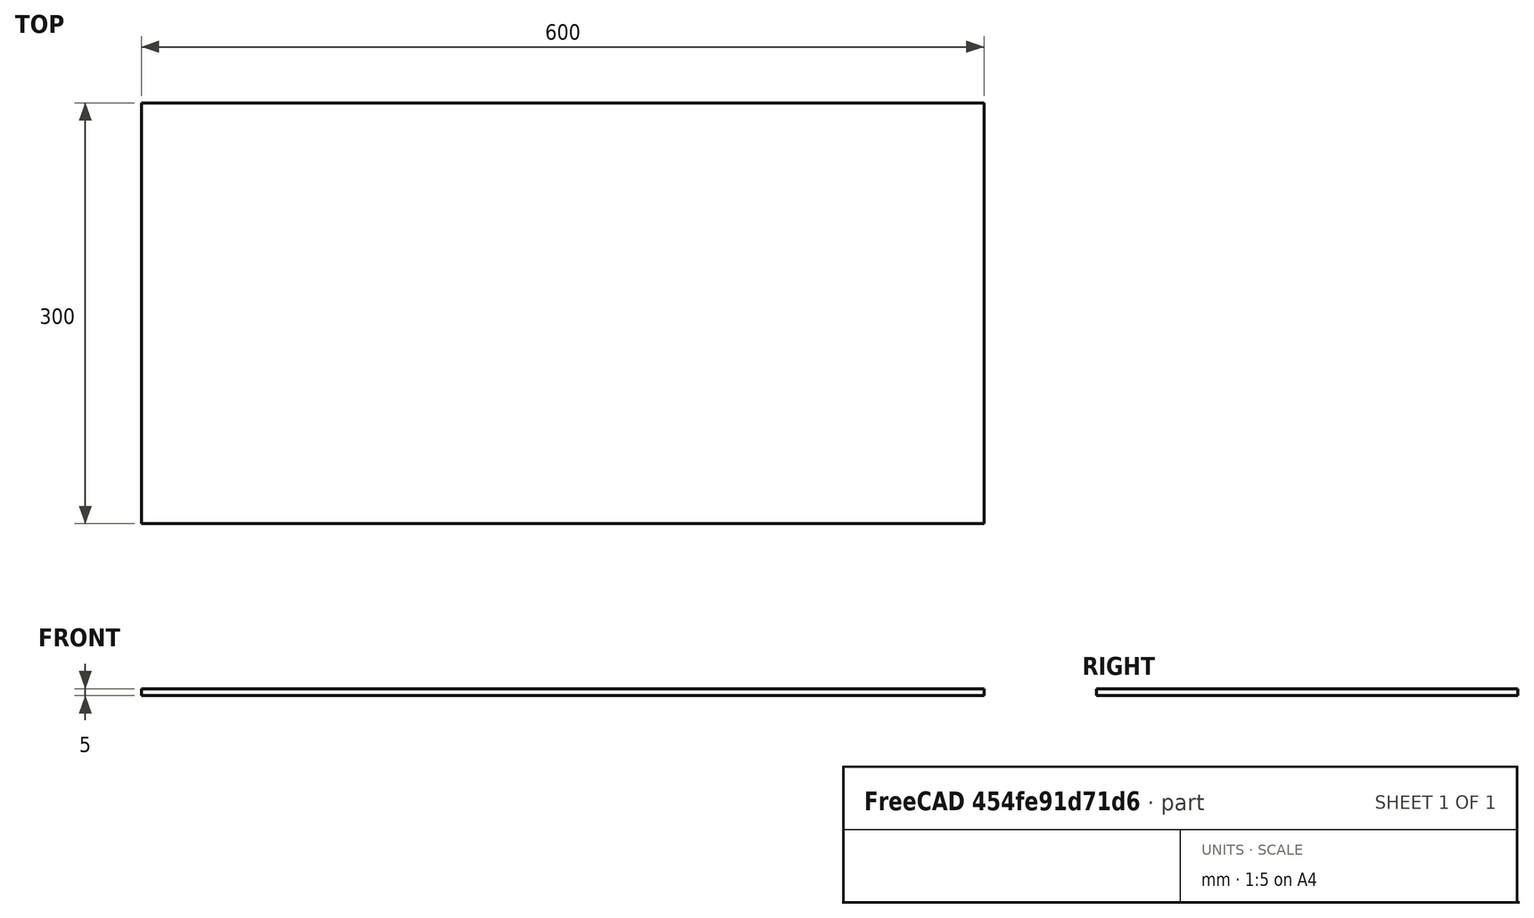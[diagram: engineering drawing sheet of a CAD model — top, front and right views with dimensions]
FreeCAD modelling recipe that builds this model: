
FCSTD DOCUMENT  (FreeCAD 0.19R16694 (Git))
Label: window-acryl-600x300
License: Public Domain
LicenseURL: http://en.wikipedia.org/wiki/Public_domain
objects: Sketcher::SketchObject×1, PartDesign::Pad×1, PartDesign::Body×1
note: 4 computed .brp shape members not serialized (recipe doc carries the construction recipe); baked Part::Feature solids carry a one-line shape summary decoded from their .brp

FEATURE [Sketcher::SketchObject] Sketch
  MapMode = 5
  Support = -> [XY_Plane]
  sketch-geometry (4):
    g0: LineSegment StartX=-300 StartY=150 StartZ=0 EndX=300 EndY=150 EndZ=0
    g1: LineSegment StartX=300 StartY=150 StartZ=0 EndX=300 EndY=-150 EndZ=0
    g2: LineSegment StartX=300 StartY=-150 StartZ=0 EndX=-300 EndY=-150 EndZ=0
    g3: LineSegment StartX=-300 StartY=-150 StartZ=0 EndX=-300 EndY=150 EndZ=0
  constraints (10):
    c: Coincident(g0,g1)
    c: Coincident(g1,g2)
    c: Coincident(g2,g3)
    c: Coincident(g3,g0)
    c: Horizontal(g2)
    c: Vertical(g1)
    c: Distance(g3) = 300
    c: Distance(g0) = 600
    c: Symmetric(g0,g0,g-2)
    c: Symmetric(g2,g0,g-1)
FEATURE [PartDesign::Pad] Pad
  Length = 5
  Length2 = 100
  Midplane = true
  Profile = -> Sketch
  Type = 0
FEATURE [PartDesign::Body] Body  label="AcrylWindow"
  Group = -> [Sketch,Pad]
  Origin = -> Origin
  Tip = -> Pad
